# Revit family: Casement_28_F_Top_Hung_Standard
name_source: partatom
category: Windows
revit_build: Autodesk Revit 2014 (Build: 20130308_1515(x64)
units: mm (PartAtom-declared; Revit-internal decimal feet)

## types (6) — shared parameters
Aluminium Thickness = 1 mm  [stored 0.00328084 ft]
Area Pane Left Bottom = 0.13 m²
Area Pane Left Top = 0.23 m²
Area Pane Right Bottom = 0.13 m²
Area Pane Right Top = 0.23 m²
Bead SG Gap = 13 mm  [stored 0.0426509 ft]
Bottom Hung = No
Casement Dimension = 28 mm  [stored 0.0918635 ft]
Custom Sash Left Height = 554 mm  [stored 1.81759 ft]
Custom Sash Left Width = 554 mm  [stored 1.81759 ft]
Custom Sash Right Height = 554 mm  [stored 1.81759 ft]
Custom Sash Right Width = 554 mm  [stored 1.81759 ft]
Custom Window Height = 890 mm  [stored 2.91995 ft]
Default Sill Height = 800 mm  [stored 2.62467 ft]
Depth Bead = 14 mm  [stored 0.0459318 ft]
Depth Mullion = 29 mm  [stored 0.0951444 ft]
Description = Window 28mm, Type F top hung
Frame Center Offset = 14 mm  [stored 0.0459318 ft]
Height = 890 mm  [stored 2.91995 ft]
Height Fixed Panel Center = 830 mm  [stored 2.7231 ft]
Height Fixed Panel Left = 260 mm  [stored 0.853018 ft]
Height Fixed Panel Right = 260 mm  [stored 0.853018 ft]
Height Sash Left = 524 mm  [stored 1.71916 ft]
Height Sash Left Opening = 554 mm  [stored 1.81759 ft]
Height Sash Right = 524 mm  [stored 1.71916 ft]
Height Sash Right Opening = 554 mm  [stored 1.81759 ft]
Length Mullion = 890 mm  [stored 2.91995 ft]
Length Transom Left = 540 mm  [stored 1.77165 ft]
Length Transom Right = 540 mm  [stored 1.77165 ft]
Limit Fixed Pane Height Max = 1800 mm  [stored 5.90551 ft]
Limit Fixed Pane Height Min = 200 mm  [stored 0.656168 ft]
Limit Fixed Pane Width Max = 1500 mm  [stored 4.92126 ft]
Limit Fixed Pane Width Min = 200 mm  [stored 0.656168 ft]
Limit Sash Height Max = 600 mm  [stored 1.9685 ft]
Limit Sash Height Min = 300 mm  [stored 0.984252 ft]
Limit Sash Width Max = 900 mm  [stored 2.95276 ft]
Limit Sash Width Min = 300 mm  [stored 0.984252 ft]
Limit Window Height Max = 1860 mm  [stored 6.10236 ft]
Limit Window Height Min = 830 mm  [stored 2.7231 ft]
Limit Window Width Max = 2700 mm
Limit Window Width Min = 1400 mm
Manufacturer = Crealco
Model = Casement 28
Mullion Depth Windload Based = 29 mm  [stored 0.0951444 ft]
Offset Bead Center Reversed = 14 mm  [stored 0.0459318 ft]
Offset Fixed Panel Center Left = 600 mm  [stored 1.9685 ft]
Offset Mullion Left = 570 mm  [stored 1.87008 ft]
Offset Mullion Right = 570 mm  [stored 1.87008 ft]
Offset Sash Side = 23 mm  [stored 0.0754593 ft]
Offset Sash Top = 23 mm  [stored 0.0754593 ft]
Offset Transom Left Top = 570 mm  [stored 1.87008 ft]
Offset Transom Right Top = 570 mm  [stored 1.87008 ft]
Offset Window Exterior = 14 mm  [stored 0.0459318 ft]
SG Gasket Thickness = 6 mm  [stored 0.019685 ft]
Sash Center Offset = 11 mm  [stored 0.0360892 ft]
Sash Overlap = 7 mm  [stored 0.0229659 ft]
Sash Spacing Inner = 8 mm  [stored 0.0262467 ft]
Single Glazing = Yes
Top Hung = Yes
URL = http://www.crealco.co.za
Wall Closure = By host
Width Bead = 15 mm  [stored 0.0492126 ft]
Width Fixed Panel Left = 540 mm  [stored 1.77165 ft]
Width Fixed Panel Right = 540 mm  [stored 1.77165 ft]
Width Profile = 30 mm  [stored 0.0984252 ft]
Width Sash Left = 524 mm  [stored 1.71916 ft]
Width Sash Left Opening = 554 mm  [stored 1.81759 ft]
Width Sash Right = 524 mm  [stored 1.71916 ft]
Width Sash Right Opening = 554 mm  [stored 1.81759 ft]
zero-valued in all types: Window Exterior Offset

## per-type parameters (varying)
| type | Area Pane Middle | Clearvue SHGC Value | Clearvue U Value | Custom Windload | Custom Window Width | Energy Advantage SHGC Value | Energy Advantage U Value | Intruderprufe LowE SHGC Value | Intruderprufe LowE U Value | Intruderprufe SHGC Value | Intruderprufe U Value | Max Pane Area | Width | Width Fixed Panel Center | Windload Design |
| 28-1809TT-1000Pa | 0.48 m² | 0.677 | 6.96 | 1000 mm  [stored 3.28084 ft] | 1790 mm  [stored 5.8727 ft] | 0.604 | 5.37 | 0.562 | 5.26 | 0.659 | 6.98 | 0.48 m² | 1790 mm  [stored 5.8727 ft] | 590 mm | 1000 mm  [stored 3.28084 ft] |
| 28-2409TT-1000Pa | 0.97 m² | 0.765 | 7.36 | 1000 mm  [stored 3.28084 ft] | 2390 mm  [stored 7.84121 ft] | 0.683 | 5.54 | 0.642 | 5.4 | 0.745 | 7.35 | 0.97 m² | 2390 mm  [stored 7.84121 ft] | 1190 mm | 1000 mm  [stored 3.28084 ft] |
| 28-2409TT-2000Pa | 0.97 m² | 0.765 | 7.45 | 1000 mm  [stored 3.28084 ft] | 2390 mm  [stored 7.84121 ft] | 0.684 | 5.64 | 0.642 | 5.5 | 0.732 | 7.37 | 0.97 m² | 2390 mm  [stored 7.84121 ft] | 1190 mm | 1000 mm  [stored 3.28084 ft] |
| 28-1809TT-1500Pa | 0.48 m² | 0.677 | 6.96 | 1500 mm  [stored 4.92126 ft] | 1790 mm  [stored 5.8727 ft] | 0.604 | 5.37 | 0.562 | 5.26 | 0.659 | 6.98 | 0.48 m² | 1790 mm  [stored 5.8727 ft] | 590 mm | 1500 mm  [stored 4.92126 ft] |
| 28-1809TT-2000Pa | 0.48 m² | 0.677 | 6.96 | 2000 mm  [stored 6.56168 ft] | 1790 mm  [stored 5.8727 ft] | 0.604 | 5.37 | 0.562 | 5.26 | 0.659 | 6.98 | 0.48 m² | 1790 mm  [stored 5.8727 ft] | 590 mm | 2000 mm  [stored 6.56168 ft] |
| 28-2409TT-1500Pa | 0.97 m² | 0.765 | 7.36 | 1500 mm  [stored 4.92126 ft] | 2390 mm  [stored 7.84121 ft] | 0.683 | 5.54 | 0.642 | 5.4 | 0.745 | 7.35 | 0.97 m² | 2390 mm  [stored 7.84121 ft] | 1190 mm | 1500 mm  [stored 4.92126 ft] |

note: [stored X ft] marks values corroborated as IEEE doubles in the binary element streams (Revit-internal decimal feet)

## geometry (parser evidence)
native form markers: Sweep x30
no freeform markers — native parametric forms only
